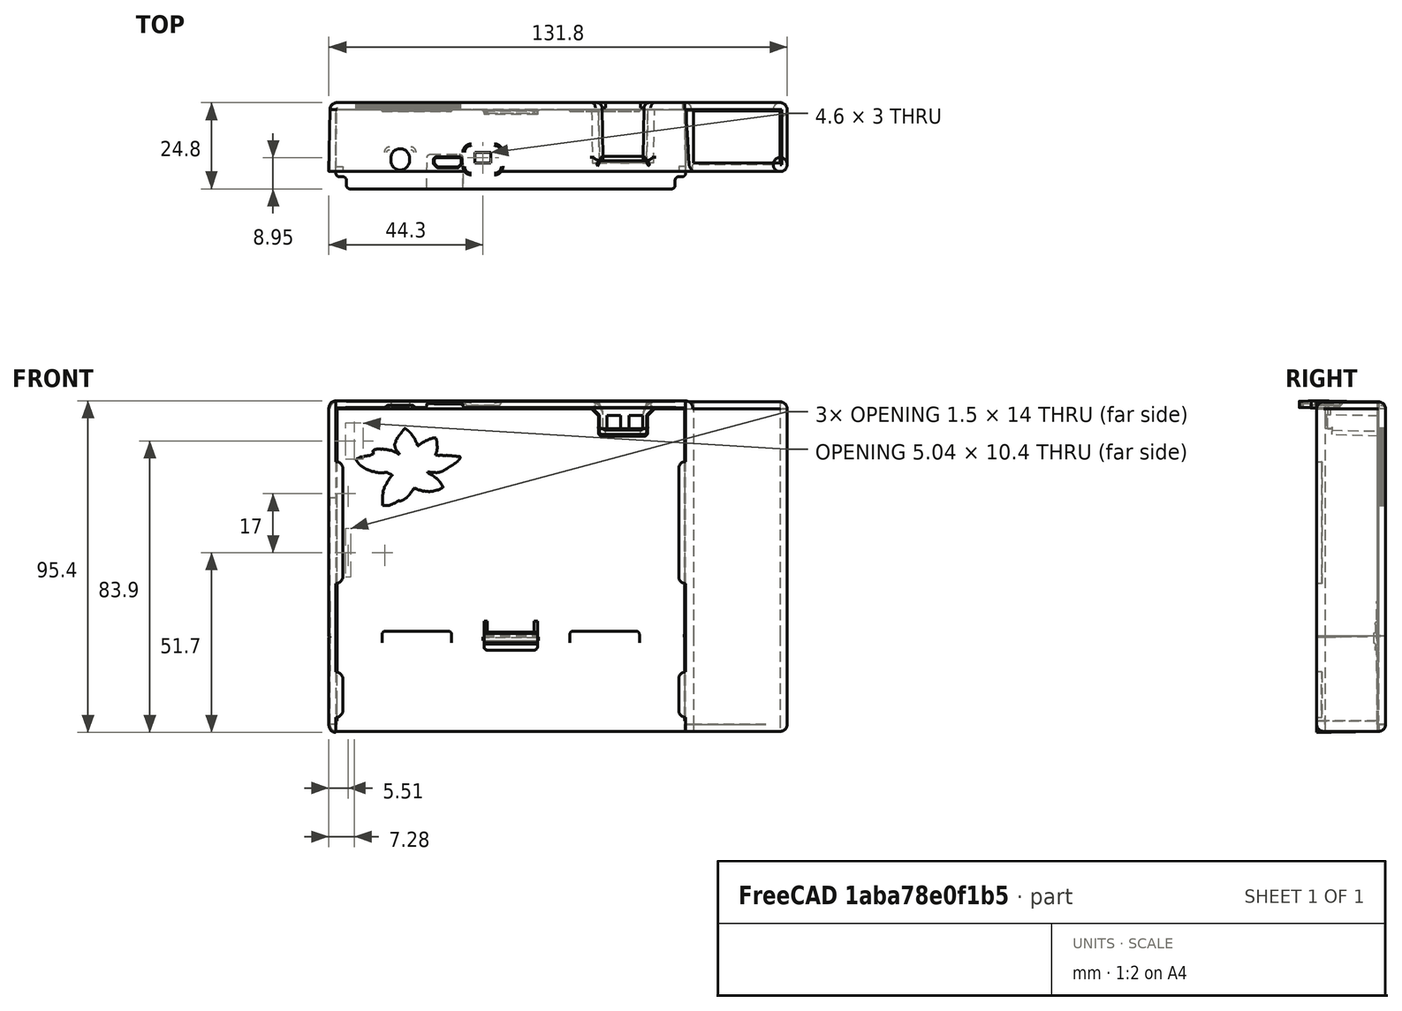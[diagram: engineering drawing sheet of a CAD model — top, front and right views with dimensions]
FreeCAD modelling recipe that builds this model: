
FCSTD DOCUMENT  (FreeCAD 0.20R29410 (Git))
Label: N2CaseOnePeice_10_18_2022
License: All rights reserved
LicenseURL: http://en.wikipedia.org/wiki/All_rights_reserved
objects: Part::Box×22, Part::Cylinder×12, Part::MultiFuse×9, Part::Cut×9, Part::Sphere×4, Part::Feature×3
note: 59 computed .brp shape members not serialized (recipe doc carries the construction recipe); baked Part::Feature solids carry a one-line shape summary decoded from their .brp

FEATURE [Part::Feature] Solid  label="N2_BOTTOM_COVER"
  shape: bbox 104.6 x 25.21 x 71.78 mm, 343 faces (baked)
FEATURE [Part::Feature] Solid001  label="N2_TOP_COVER"
  shape: bbox 104.6 x 24.81 x 29.22 mm, 349 faces (baked)
FEATURE [Part::Box] Box  label="Cube"
  AttacherType = Attacher::AttachEngine3D
  Height = 15
  Length = 62.5
  Placement = pos=(-49,18,44) rot=(0,1,0;1.5708rad)
  Width = 2
FEATURE [Part::MultiFuse] Fusion  label="BottomCover"
  Shapes = -> [Solid,Box]
FEATURE [Part::Box] Box001  label="Cube001"
  AttacherType = Attacher::AttachEngine3D
  Height = 15
  Length = 97.5
  Placement = pos=(48.5,20,-3.5) rot=(0,1,0;3.14159rad)
  Width = 2
FEATURE [Part::Cut] Cut
  Base = -> Fusion
  Tool = -> Box001
FEATURE [Part::Box] Box002  label="usbEthernet"
  AttacherType = Attacher::AttachEngine3D
  Height = 25
  Length = 72
  Placement = pos=(52.5,2.6,47.4) rot=(0,1,0;1.5708rad)
  Width = 15
FEATURE [Part::Box] Box003  label="usbEthernetCover"
  AttacherType = Attacher::AttachEngine3D
  Height = 27.5
  Length = 72
  Placement = pos=(50.5,2.2,47.4) rot=(0,1,0;1.5708rad)
  Width = 15.85
FEATURE [Part::Box] Box004  label="usbEthernetCover001"
  AttacherType = Attacher::AttachEngine3D
  Height = 27.52
  Length = 65.19
  Placement = pos=(49.98,17.6,45.39) rot=(0,1,0;1.5708rad)
  Width = 2.4
FEATURE [Part::Box] Box005  label="usbEthernetCover002"
  AttacherType = Attacher::AttachEngine3D
  Height = 2
  Length = 65.19
  Placement = pos=(77.5,2.2,45.39) rot=(0,1,0;1.5708rad)
  Width = 15.8
FEATURE [Part::Cylinder] Cylinder
  Angle = 90
  AttacherType = Attacher::AttachEngine3D
  FirstAngle = 0
  Height = 65.2
  Placement = pos=(77.5,2.2,-19.8) rot=(0,0,-1;1.5708rad)
  Radius = 2
  SecondAngle = 0
FEATURE [Part::Cylinder] Cylinder001
  Angle = 90
  AttacherType = Attacher::AttachEngine3D
  FirstAngle = 0
  Height = 27.5
  Placement = pos=(77.5,18,45.4) rot=(0,-1,0;1.5708rad)
  Radius = 2
  SecondAngle = 0
FEATURE [Part::Cylinder] Cylinder002
  Angle = 90
  AttacherType = Attacher::AttachEngine3D
  FirstAngle = 0
  Height = 15.8
  Placement = pos=(77.5,2.2,45.4) rot=(0.57735,0.57735,0.57735;4.18879rad)
  Radius = 2
  SecondAngle = 0
FEATURE [Part::Cylinder] Cylinder003
  Angle = 90
  AttacherType = Attacher::AttachEngine3D
  FirstAngle = 0
  Height = 65.2
  Placement = pos=(77.5,18,-19.8) rot=(0,0,1;0rad)
  Radius = 2
  SecondAngle = 0
FEATURE [Part::Box] Box006  label="usbEthernetCover003"
  AttacherType = Attacher::AttachEngine3D
  Height = 27.2
  Length = 65.19
  Placement = pos=(50.3,0.2,45.39) rot=(0,1,0;1.5708rad)
  Width = 2.4
FEATURE [Part::Cylinder] Cylinder004
  Angle = 90
  AttacherType = Attacher::AttachEngine3D
  FirstAngle = 0
  Height = 26.4
  Placement = pos=(77.5,2.2,45.4) rot=(0.57735,-0.57735,-0.57735;2.0944rad)
  Radius = 2
  SecondAngle = 0
FEATURE [Part::Sphere] Sphere
  Angle1 = -90
  Angle2 = 90
  Angle3 = 360
  AttacherType = Attacher::AttachEngine3D
  Placement = pos=(77.5,18,45.4) rot=(0,0,1;0rad)
  Radius = 2
FEATURE [Part::Sphere] Sphere001
  Angle1 = -90
  Angle2 = 90
  Angle3 = 360
  AttacherType = Attacher::AttachEngine3D
  Placement = pos=(77.5,2.2,45.4) rot=(0,0,1;0rad)
  Radius = 2
FEATURE [Part::MultiFuse] Fusion001  label="usbCover"
  Shapes = -> [Box003,Box004,Box005,Cylinder,Cylinder001,Cylinder002,Cylinder003,Box006,Cylinder004,Sphere,Sphere001]
FEATURE [Part::MultiFuse] Fusion002
  Shapes = -> [Cut,Fusion001]
FEATURE [Part::Cut] Cut001  label="front"
  Base = -> Fusion002
  Tool = -> Box002
FEATURE [Part::Box] Box007  label="Cube002"
  AttacherType = Attacher::AttachEngine3D
  Height = 10
  Length = 30
  Placement = pos=(79.5,0,-19.8) rot=(0,1,0;3.14159rad)
  Width = 20
FEATURE [Part::Cut] Cut002
  Base = -> Cut001
  Tool = -> Box007
FEATURE [Part::Box] Box008  label="Cube003"
  AttacherType = Attacher::AttachEngine3D
  Height = 10
  Length = 30
  Placement = pos=(79.5,0,-19.8) rot=(0,1,0;3.14159rad)
  Width = 20
FEATURE [Part::Cut] Cut003  label="front001"
  Base = -> Cut002
  Tool = -> Box008
FEATURE [Part::Box] Box009  label="usbEthernet001"
  AttacherType = Attacher::AttachEngine3D
  Height = 25
  Length = 72
  Placement = pos=(52.5,2.6,6.3) rot=(0,1,0;1.5708rad)
  Width = 15
FEATURE [Part::Box] Box010  label="usbEthernetCover004"
  AttacherType = Attacher::AttachEngine3D
  Height = 27.5
  Length = 72
  Placement = pos=(50.5,2.2,-19.8) rot=(0,1,0;1.5708rad)
  Width = 15.85
FEATURE [Part::Box] Box011  label="usbEthernetCover005"
  AttacherType = Attacher::AttachEngine3D
  Height = 27.52
  Length = 65.19
  Placement = pos=(49.98,17.6,-19.8) rot=(0,1,0;1.5708rad)
  Width = 2.4
FEATURE [Part::Box] Box012  label="usbEthernetCover006"
  AttacherType = Attacher::AttachEngine3D
  Height = 2
  Length = 65.19
  Placement = pos=(77.5,2.2,-19.8) rot=(0,1,0;1.5708rad)
  Width = 15.8
FEATURE [Part::Box] Box013  label="usbEthernetCover007"
  AttacherType = Attacher::AttachEngine3D
  Height = 27.2
  Length = 65.19
  Placement = pos=(50.3,0.2,-19.8) rot=(0,1,0;1.5708rad)
  Width = 2.4
FEATURE [Part::Box] Box016  label="Cube005"
  AttacherType = Attacher::AttachEngine3D
  Height = 50
  Length = 29.5
  Placement = pos=(79.5,0,-45.4) rot=(0,1,0;3.14159rad)
  Width = 20
FEATURE [Part::MultiFuse] Fusion003
  Shapes = -> [Solid001,Box010,Box011,Box012,Box013]
FEATURE [Part::Cut] Cut004
  Base = -> Fusion003
  Tool = -> Box016
FEATURE [Part::Cut] Cut005
  Base = -> Cut004
  Tool = -> Box009
FEATURE [Part::Box] Box017  label="Cube006"
  AttacherType = Attacher::AttachEngine3D
  Height = 50
  Length = 23.5
  Placement = pos=(73.4,17.6,-45.39) rot=(0,1,0;3.14159rad)
  Width = 20
FEATURE [Part::Cut] Cut006
  Base = -> Cut005
  Tool = -> Box017
FEATURE [Part::Cylinder] Cylinder005
  Angle = 90
  AttacherType = Attacher::AttachEngine3D
  FirstAngle = 0
  Height = 65.2
  Placement = pos=(77.5,2.2,-45.4) rot=(0,0,-1;1.5708rad)
  Radius = 2
  SecondAngle = 0
FEATURE [Part::Cylinder] Cylinder006
  Angle = 90
  AttacherType = Attacher::AttachEngine3D
  FirstAngle = 0
  Height = 27.5
  Placement = pos=(77.5,18,-45.4) rot=(0,-1,0;1.5708rad)
  Radius = 2
  SecondAngle = 0
FEATURE [Part::Cylinder] Cylinder007
  Angle = 90
  AttacherType = Attacher::AttachEngine3D
  FirstAngle = 0
  Height = 15.8
  Placement = pos=(77.5,2.2,-45.4) rot=(-1,0,0;1.5708rad)
  Radius = 2
  SecondAngle = 0
FEATURE [Part::Cylinder] Cylinder008
  Angle = 90
  AttacherType = Attacher::AttachEngine3D
  FirstAngle = 0
  Height = 65.2
  Placement = pos=(77.5,18,-45.4) rot=(0,0,1;0rad)
  Radius = 2
  SecondAngle = 0
FEATURE [Part::Cylinder] Cylinder009
  Angle = 90
  AttacherType = Attacher::AttachEngine3D
  FirstAngle = 0
  Height = 27.6
  Placement = pos=(77.5,2.2,-45.4) rot=(0.707107,0,-0.707107;3.14159rad)
  Radius = 2
  SecondAngle = 0
FEATURE [Part::Cylinder] Cylinder010
  Angle = 90
  AttacherType = Attacher::AttachEngine3D
  FirstAngle = 0
  Height = 27.6
  Placement = pos=(77.5,18,-45.4) rot=(0.57735,0.57735,-0.57735;4.18879rad)
  Radius = 2
  SecondAngle = 0
FEATURE [Part::Box] Box018  label="Cube007"
  AttacherType = Attacher::AttachEngine3D
  Height = 2
  Length = 27.6
  Placement = pos=(49.9,18,-45.4) rot=(1,0,0;3.14159rad)
  Width = 15.8
FEATURE [Part::Box] Box019  label="usbEthernet002"
  AttacherType = Attacher::AttachEngine3D
  Height = 25
  Length = 72
  Placement = pos=(52.5,2.6,-2.5) rot=(0,1,0;1.5708rad)
  Width = 15
FEATURE [Part::Sphere] Sphere002
  Angle1 = -90
  Angle2 = 90
  Angle3 = 360
  AttacherType = Attacher::AttachEngine3D
  Placement = pos=(77.5,18,-45.4) rot=(0,0,1;0rad)
  Radius = 2
FEATURE [Part::Sphere] Sphere003
  Angle1 = -90
  Angle2 = 90
  Angle3 = 360
  AttacherType = Attacher::AttachEngine3D
  Placement = pos=(77.5,2.2,-45.4) rot=(0,0,1;0rad)
  Radius = 2
FEATURE [Part::Box] Box020  label="Cube008"
  AttacherType = Attacher::AttachEngine3D
  Height = 40
  Length = 10
  Placement = pos=(73.6,0,-19.8) rot=(0,0,1;0rad)
  Width = 22
FEATURE [Part::MultiFuse] Fusion004  label="cuts"
  Shapes = -> [Box020,Box019]
FEATURE [Part::MultiFuse] Fusion005
  Shapes = -> [Sphere003,Cut006,Cylinder005,Cylinder006,Cylinder007,Cylinder008,Cylinder009,Cylinder010,Box018,Sphere002]
FEATURE [Part::Cut] Cut007  label="back"
  Base = -> Fusion005
  Tool = -> Fusion004
FEATURE [Part::Box] Box021  label="Cube009"
  AttacherType = Attacher::AttachEngine3D
  Height = 32.5
  Length = 97.5
  Placement = pos=(48.5,18,-11.9) rot=(0,1,0;3.14159rad)
  Width = 2
FEATURE [Part::MultiFuse] Fusion006  label="back001"
  Shapes = -> [Cut007,Box021]
FEATURE [Part::Cylinder] Cylinder011
  Angle = 90
  AttacherType = Attacher::AttachEngine3D
  FirstAngle = 0
  Height = 65.2
  Placement = pos=(-50,18,-45.4) rot=(0,0,1;1.5708rad)
  Radius = 2
  SecondAngle = 0
FEATURE [Part::Box] Box070  label="Cube010"
  AttacherType = Attacher::AttachEngine3D
  Height = 20
  Length = 1.7
  Placement = pos=(-50.3,0.2,-10) rot=(0,1,0;3.14159rad)
  Width = 17.8
FEATURE [Part::Box] Box071  label="cuts001"
  AttacherType = Attacher::AttachEngine3D
  Height = 10
  Length = 23
  Placement = pos=(50.3,-5,-54.4) rot=(0,0,1;1.5708rad)
  Width = 100.6
FEATURE [Part::Feature] logo3mmWidth001_solid001  label="logo3mmWidth001 (Solid)001"
  Placement = pos=(-47.5,15.27,43.04) rot=(-1,0,0;1.5708rad)
  shape: bbox 30 x 4.944 x 22.21 mm, 7244 faces (baked)
FEATURE [Part::MultiFuse] Fusion007
  Shapes = -> [Cut003,Fusion006,Cylinder011,Box070]
FEATURE [Part::MultiFuse] Fusion008
  Shapes = -> [logo3mmWidth001_solid001,Box071]
FEATURE [Part::Cut] Cut008  label="n2Case"
  Base = -> Fusion007
  Tool = -> Fusion008
